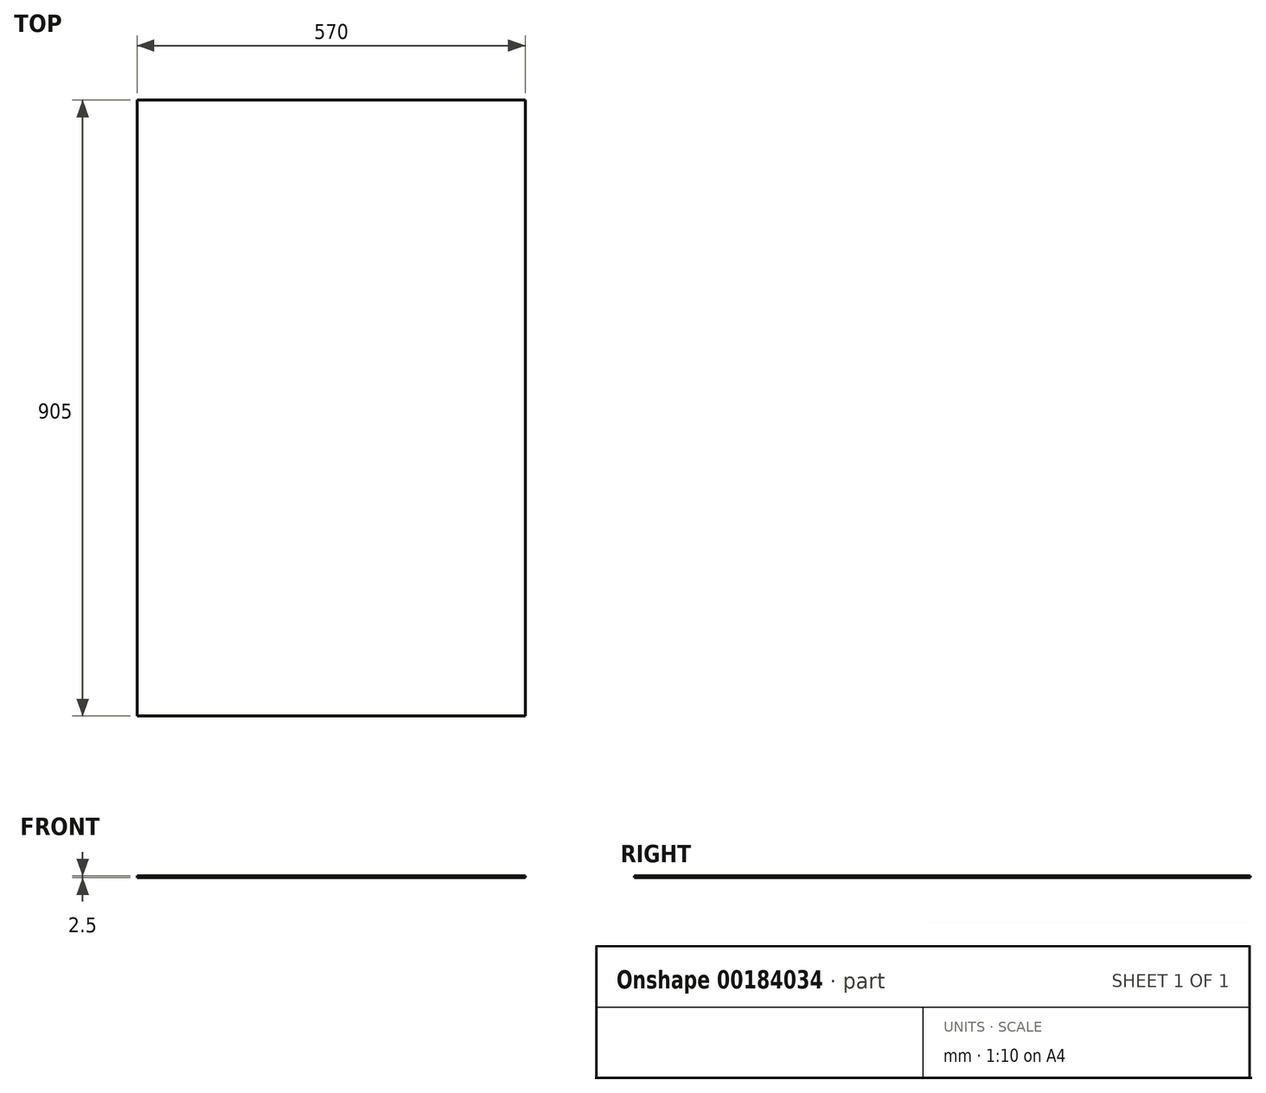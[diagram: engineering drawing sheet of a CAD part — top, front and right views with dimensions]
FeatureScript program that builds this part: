
annotation { "Feature Type Name" : "Feature", "Feature Type Description" : "" }
export const myFeature = defineFeature(function(context is Context, id is Id, definition is map)
    precondition{}
    {
        {
            var Q0;
            Q0=qCreatedBy(makeId("Top.planeOp"),FACE);
            var sketch = newSketch(context, id + "F0", { "sketchPlane" : qUnion([Q0])});
            skLineSegment(sketch, "E0.bottom", {"start": v(285, 452.5) * mm, "end": v(-285, 452.5) * mm});
            skLineSegment(sketch, "E0.top", {"start": v(285, -452.5) * mm, "end": v(-285, -452.5) * mm});
            skLineSegment(sketch, "E0.left", {"start": v(285, 452.5) * mm, "end": v(285, -452.5) * mm});
            skLineSegment(sketch, "E0.right", {"start": v(-285, 452.5) * mm, "end": v(-285, -452.5) * mm});
            skPoint(sketch, "E0.middle", {"position": v(0, 0) * mm});
            skSolve(sketch);
        }
        {
            var Q0;
            Q0 = qSketchRegion(id + "F0", true);
            extrude(context, id + "F1", {"entities" : qUnion([Q0]), "depth" : 2.5 * mm});
        }
    });
